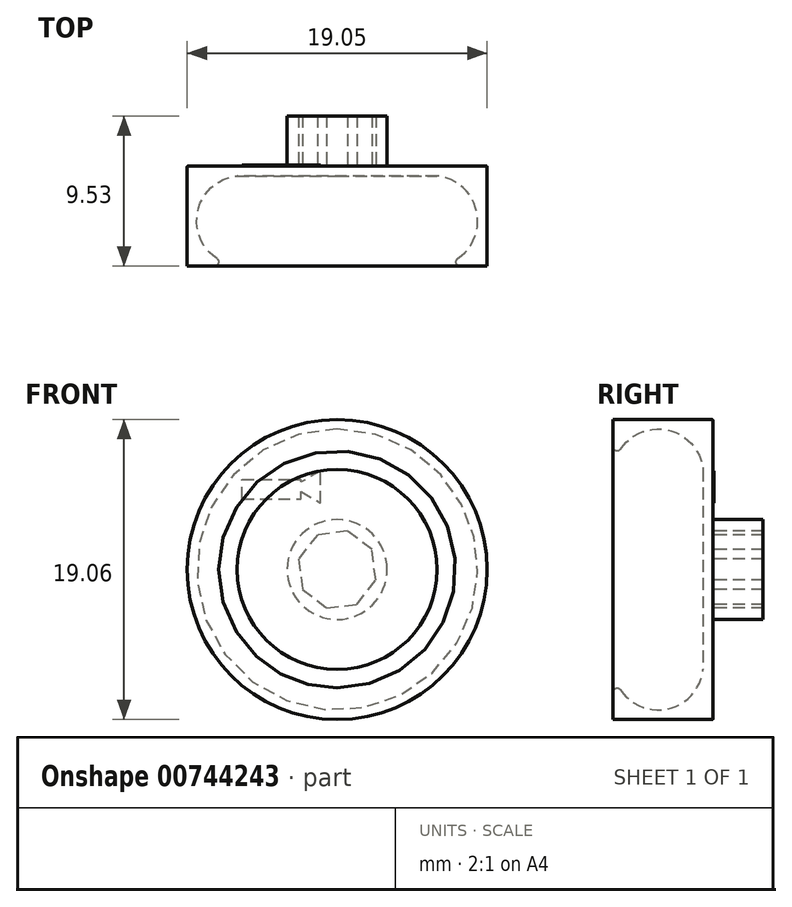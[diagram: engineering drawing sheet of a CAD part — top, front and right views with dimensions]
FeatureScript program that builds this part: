
annotation { "Feature Type Name" : "Feature", "Feature Type Description" : "" }
export const myFeature = defineFeature(function(context is Context, id is Id, definition is map)
    precondition{}
    {
        {
            var Q0;
            Q0=qCreatedBy(makeId("Top.planeOp"),FACE);
            var sketch = newSketch(context, id + "F0", { "sketchPlane" : qUnion([Q0])});
            skLineSegment(sketch, "E0.bottom", {"start": v(-37.44, -13.4) * mm, "end": v(-27.91, -13.4) * mm});
            skLineSegment(sketch, "E0.top", {"start": v(-37.44, -19.76) * mm, "end": v(-27.91, -19.76) * mm});
            skLineSegment(sketch, "E0.left", {"start": v(-37.44, -13.4) * mm, "end": v(-37.44, -19.76) * mm});
            skLineSegment(sketch, "E0.right", {"start": v(-27.91, -13.4) * mm, "end": v(-27.91, -19.76) * mm});
            skArc(sketch, "E1", {"start": v(-34.26, -14.04) * mm, "mid": v(-36.83, -16.9) * mm, "end": v(-34.26, -19.76) * mm});
            skLineSegment(sketch, "E2", {"start": v(-34.26, -14.04) * mm, "end": v(-27.91, -14.04) * mm});
            skSolve(sketch);
        }
        {
            var Q0;
            {var subQ1=sQuery(id+"F0.wireOp",EDGE,"E0.bottom");Q0=makeQuery(id+"F0.imprint","IMPRINT",FACE,{"disambiguationData":[TD([[makeQuery(id+"F0.imprint","IMPRINT",EDGE,{"derivedFrom":subQ1}),-1.0]])]});}
            var Q1;
            Q1=sQuery(id+"F0.wireOp",EDGE,"E0.right");
            revolve(context, id + "F1", {"surfaceOperationType" : NewSurfaceOperationType.NEW, "entities" : qUnion([Q0]), "axis" : qUnion([Q1]), "revolveType" : RevolveType.FULL});
        }
        {
            var Q0;
            Q0=makeQuery(id+"F1.opRevolve","SWEPT_FACE",FACE,{"disambiguationData":[OSD([sQuery(id+"F0.wireOp",EDGE,"E0.bottom")])]});
            var sketch = newSketch(context, id + "F2", { "sketchPlane" : qUnion([Q0])});
            skCircle(sketch, "E3", {"center": v(27.91, 0) * mm, "radius": 3.17 * mm});
            skCircle(sketch, "E4.cCircle", {"center": v(27.91, 0) * mm, "radius": 2.54 * mm, "construction": true});
            skLineSegment(sketch, "E4.0", {"start": v(28.58, -2.45) * mm, "end": v(26.65, -2.2) * mm});
            skLineSegment(sketch, "E4.1", {"start": v(26.65, -2.2) * mm, "end": v(25.46, -0.67) * mm});
            skLineSegment(sketch, "E4.2", {"start": v(25.46, -0.67) * mm, "end": v(25.7, 1.26) * mm});
            skLineSegment(sketch, "E4.3", {"start": v(25.7, 1.26) * mm, "end": v(27.25, 2.45) * mm});
            skLineSegment(sketch, "E4.4", {"start": v(27.25, 2.45) * mm, "end": v(29.17, 2.2) * mm});
            skLineSegment(sketch, "E4.5", {"start": v(29.17, 2.2) * mm, "end": v(30.36, 0.67) * mm});
            skLineSegment(sketch, "E4.6", {"start": v(30.36, 0.67) * mm, "end": v(30.12, -1.26) * mm});
            skLineSegment(sketch, "E4.7", {"start": v(30.12, -1.26) * mm, "end": v(28.58, -2.45) * mm});
            skSolve(sketch);
        }
        {
            var Q0;
            Q0=makeQuery(id+"F2.imprint","IMPRINT",FACE,{"disambiguationData":[TD([[makeQuery(id+"F2.imprint","IMPRINT",EDGE,{"derivedFrom":sQuery(id+"F2.wireOp",EDGE,"E3")}),1.0]])]});
            extrude(context, id + "F3", {"entities" : qUnion([Q0]), "operationType" : NewBodyOperationType.ADD, "depth" : 3.17 * mm, "offsetDistance" : 25.4 * mm});
        }
        {
            var Q0;
            Q0=makeQuery(id+"F1.opRevolve","SWEPT_EDGE",EDGE,{"disambiguationData":[OSD([sQuery(id+"F0.wireOp",EDGE,"E0.bottom"),sQuery(id+"F0.wireOp",EDGE,"E0.left")])]});
            fillet(context, id + "F4", {"entities" : qUnion([Q0]), "radius" : 0.06 * mm, "tangentPropagation" : true, "allowEdgeOverflow" : false});
        }
        {
            var Q0;
            Q0=makeQuery(id+"F1.opRevolve","SWEPT_EDGE",EDGE,{"disambiguationData":[OSD([sQuery(id+"F0.wireOp",EDGE,"E0.top"),sQuery(id+"F0.wireOp",EDGE,"E1")])]});
            fillet(context, id + "F5", {"entities" : qUnion([Q0]), "radius" : 0.25 * mm, "tangentPropagation" : true, "allowEdgeOverflow" : false});
        }
        {
            var Q0;
            Q0=makeQuery(id+"F3.boolean.opBoolean","SPLIT",FACE,{"disambiguationData":[TD([makeQuery(id+"F1.opRevolve","SWEPT_FACE",FACE,{"disambiguationData":[OSD([sQuery(id+"F0.wireOp",EDGE,"E0.left")])]})])],"derivedFrom":makeQuery(id+"F1.opRevolve","SWEPT_FACE",FACE,{"disambiguationData":[OSD([sQuery(id+"F0.wireOp",EDGE,"E0.bottom")])]})});
            var sketch = newSketch(context, id + "F6", { "sketchPlane" : qUnion([Q0])});
            skLineSegment(sketch, "E5.bottom", {"start": v(33.95, 4.5) * mm, "end": v(30.21, 4.5) * mm});
            skLineSegment(sketch, "E5.top", {"start": v(33.95, 5.72) * mm, "end": v(30.21, 5.72) * mm});
            skLineSegment(sketch, "E5.left", {"start": v(33.95, 4.5) * mm, "end": v(33.95, 5.72) * mm});
            skLineSegment(sketch, "E5.right", {"start": v(30.21, 4.5) * mm, "end": v(30.21, 5.72) * mm});
            skCircle(sketch, "E6.cCircle", {"center": v(29.56, 5.26) * mm, "radius": 1.18 * mm, "construction": true});
            skLineSegment(sketch, "E6.0", {"start": v(28.97, 4.23) * mm, "end": v(28.96, 6.28) * mm});
            skLineSegment(sketch, "E6.1", {"start": v(28.96, 6.28) * mm, "end": v(30.74, 5.26) * mm});
            skLineSegment(sketch, "E6.2", {"start": v(30.74, 5.26) * mm, "end": v(28.97, 4.23) * mm});
            skSolve(sketch);
        }
        {
            var Q0;
            {var subQ1=sQuery(id+"F6.wireOp",EDGE,"E5.bottom");Q0=makeQuery(id+"F6.imprint","IMPRINT",FACE,{"disambiguationData":[TD([[makeQuery(id+"F6.imprint","IMPRINT",EDGE,{"derivedFrom":subQ1}),-1.0]])]});}
            var Q1;
            {var subQ0=sQuery(id+"F6.wireOp",EDGE,"E6.2");var subQ1=sQuery(id+"F6.wireOp",EDGE,"E5.right");var subQ2=makeQuery(id+"F6.imprint","INTERSECT",VERTEX,{"derivedFrom":[subQ1,subQ0]});Q1=makeQuery(id+"F6.imprint","IMPRINT",FACE,{"disambiguationData":[TD([[makeQuery(id+"F6.imprint","IMPRINT",EDGE,{"disambiguationData":[TD([[subQ2,-1.0]])],"derivedFrom":subQ1}),-1.0]])]});}
            var Q2;
            {var subQ5=sQuery(id+"F6.wireOp",EDGE,"E6.0");Q2=makeQuery(id+"F6.imprint","IMPRINT",FACE,{"disambiguationData":[TD([[makeQuery(id+"F6.imprint","IMPRINT",EDGE,{"derivedFrom":subQ5}),-1.0]])]});}
            extrude(context, id + "F7", {"entities" : qUnion([Q0, Q1, Q2]), "operationType" : NewBodyOperationType.ADD, "depth" : 0.06 * mm, "offsetDistance" : 25.4 * mm});
        }
    });
